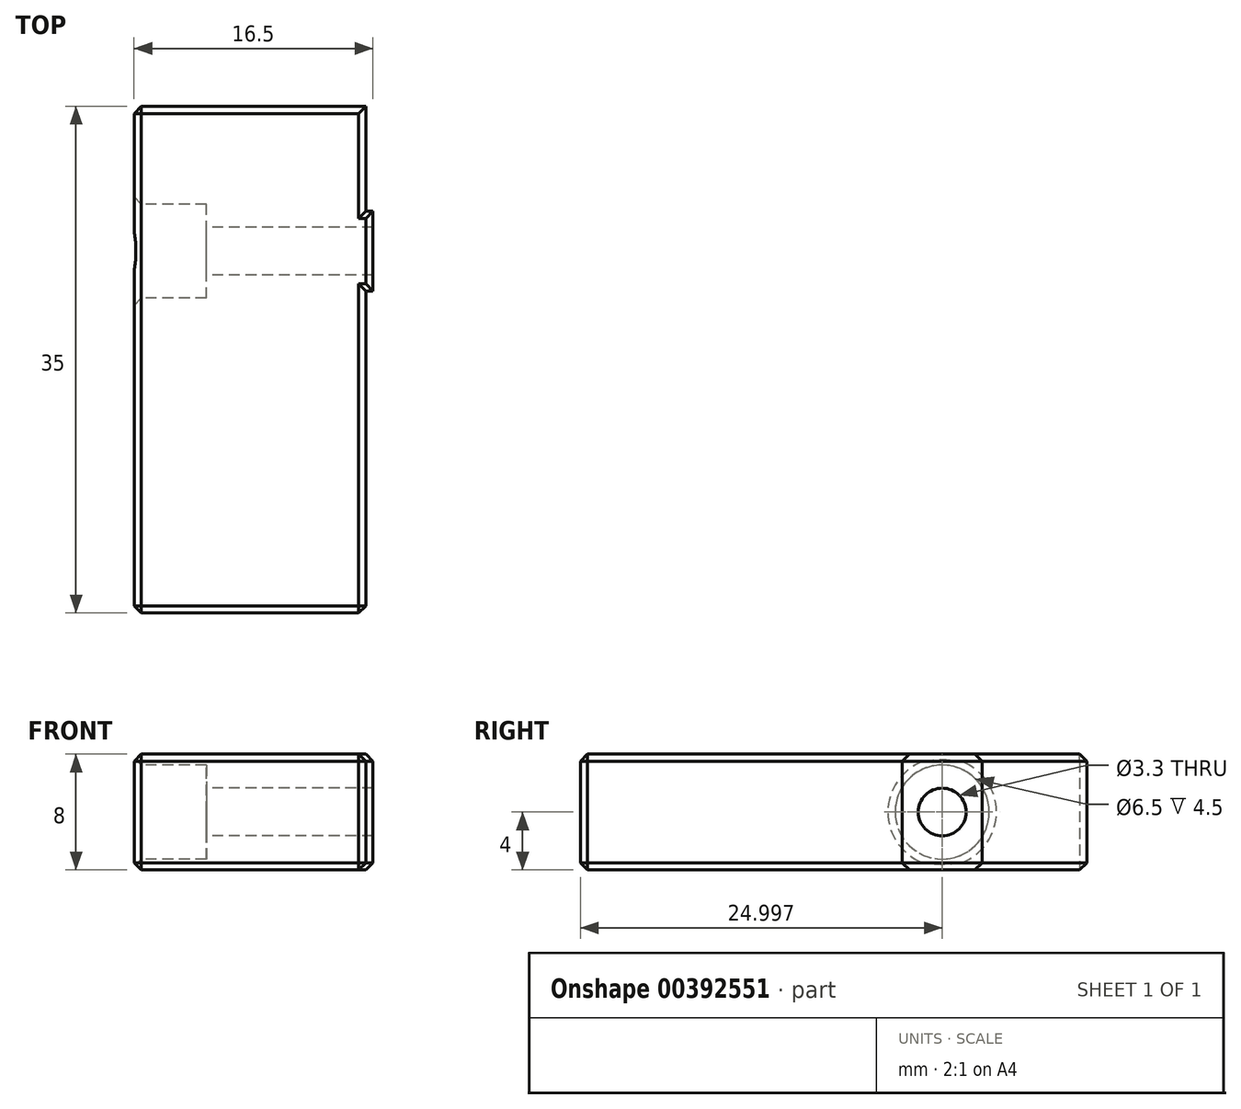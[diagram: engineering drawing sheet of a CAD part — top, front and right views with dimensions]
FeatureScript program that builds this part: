
annotation { "Feature Type Name" : "Feature", "Feature Type Description" : "" }
export const myFeature = defineFeature(function(context is Context, id is Id, definition is map)
    precondition{}
    {
        {
            var Q0;
            Q0=qCreatedBy(makeId("Top.planeOp"),FACE);
            var sketch = newSketch(context, id + "F0", { "sketchPlane" : qUnion([Q0])});
            skLineSegment(sketch, "E0", {"start": v(5.26, 14.6) * mm, "end": v(-10.74, 14.6) * mm});
            skLineSegment(sketch, "E1", {"start": v(-10.74, 14.6) * mm, "end": v(-10.74, -20.4) * mm});
            skLineSegment(sketch, "E2", {"start": v(-10.74, -20.4) * mm, "end": v(5.26, -20.4) * mm});
            skLineSegment(sketch, "E3", {"start": v(5.26, -20.4) * mm, "end": v(5.26, 14.6) * mm});
            skLineSegment(sketch, "E4", {"start": v(5.26, 7.36) * mm, "end": v(5.76, 7.36) * mm});
            skLineSegment(sketch, "E5", {"start": v(5.76, 7.36) * mm, "end": v(5.76, 1.86) * mm});
            skLineSegment(sketch, "E6", {"start": v(5.76, 1.86) * mm, "end": v(5.26, 1.86) * mm});
            skPoint(sketch, "E7", {"position": v(5.76, 4.6) * mm});
            skSolve(sketch);
        }
        {
            var Q0;
            Q0 = qSketchRegion(id + "F0", true);
            extrude(context, id + "F1", {"entities" : qUnion([Q0]), "depth" : 8 * mm});
        }
        {
            var Q0;
            Q0=makeQuery(id+"F1.opExtrude","SWEPT_FACE",FACE,{"disambiguationData":[OSD([sQuery(id+"F0.wireOp",EDGE,"E1")])]});
            var sketch = newSketch(context, id + "F2", { "sketchPlane" : qUnion([Q0])});
            skLineSegment(sketch, "E8", {"start": v(-7.36, 8) * mm, "end": v(-1.86, 0) * mm, "construction": true});
            skLineSegment(sketch, "E9", {"start": v(-1.86, 0) * mm, "end": v(-7.36, 0) * mm, "construction": true});
            skLineSegment(sketch, "E10", {"start": v(-7.36, 0) * mm, "end": v(-1.86, 8) * mm, "construction": true});
            skPoint(sketch, "E11", {"position": v(-4.6, 4) * mm});
            skSolve(sketch);
        }
        {
            var Q0;
            Q0=sQuery(id+"F2.wireOp",VERTEX,"E11");
            var Q1;
            Q1=makeQuery(id+"F1.opExtrude","SWEPT_BODY",BODY,{"disambiguationData":[OSD([sQuery(id+"F0.wireOp",EDGE,"E0"),sQuery(id+"F0.wireOp",EDGE,"E1"),sQuery(id+"F0.wireOp",EDGE,"E2"),sQuery(id+"F0.wireOp",EDGE,"E3"),sQuery(id+"F0.wireOp",EDGE,"E4"),sQuery(id+"F0.wireOp",EDGE,"E5"),sQuery(id+"F0.wireOp",EDGE,"E6")])]});
            hole(context, id + "F3", {"style" : HoleStyle.C_BORE, "endStyle" : HoleEndStyle.THROUGH, "holeDiameter" : 3.3 * mm, "cBoreDiameter" : 6.5 * mm, "cBoreDepth" : 5 * mm, "isTappedThrough" : true, "tappedDepth" : 15 * mm, "tapClearance" : 0, "startFromSketch" : true, "locations" : qUnion([Q0]), "scope" : qUnion([Q1])});
        }
        {
            var Q0;
            Q0=makeQuery(id+"F1.opExtrude","CAP_FACE",FACE,{"disambiguationData":[OSD([sQuery(id+"F0.wireOp",EDGE,"E0"),sQuery(id+"F0.wireOp",EDGE,"E1"),sQuery(id+"F0.wireOp",EDGE,"E2"),sQuery(id+"F0.wireOp",EDGE,"E3"),sQuery(id+"F0.wireOp",EDGE,"E4"),sQuery(id+"F0.wireOp",EDGE,"E5"),sQuery(id+"F0.wireOp",EDGE,"E6")])],"isStart":false});
            var Q1;
            Q1=makeQuery(id+"F1.opExtrude","SWEPT_FACE",FACE,{"disambiguationData":[OSD([sQuery(id+"F0.wireOp",EDGE,"E1")])]});
            var Q2;
            Q2=makeQuery(id+"F1.opExtrude","CAP_FACE",FACE,{"disambiguationData":[OSD([sQuery(id+"F0.wireOp",EDGE,"E0"),sQuery(id+"F0.wireOp",EDGE,"E1"),sQuery(id+"F0.wireOp",EDGE,"E2"),sQuery(id+"F0.wireOp",EDGE,"E3"),sQuery(id+"F0.wireOp",EDGE,"E4"),sQuery(id+"F0.wireOp",EDGE,"E5"),sQuery(id+"F0.wireOp",EDGE,"E6")])],"isStart":true});
            var Q3;
            Q3=makeQuery(id+"F1.opExtrude","SWEPT_FACE",FACE,{"disambiguationData":[OSD([sQuery(id+"F0.wireOp",EDGE,"E2")])]});
            chamfer(context, id + "F4", {"entities" : qUnion([Q0, Q1, Q2, Q3]), "width" : .5 * mm, "tangentPropagation" : true});
        }
    });
